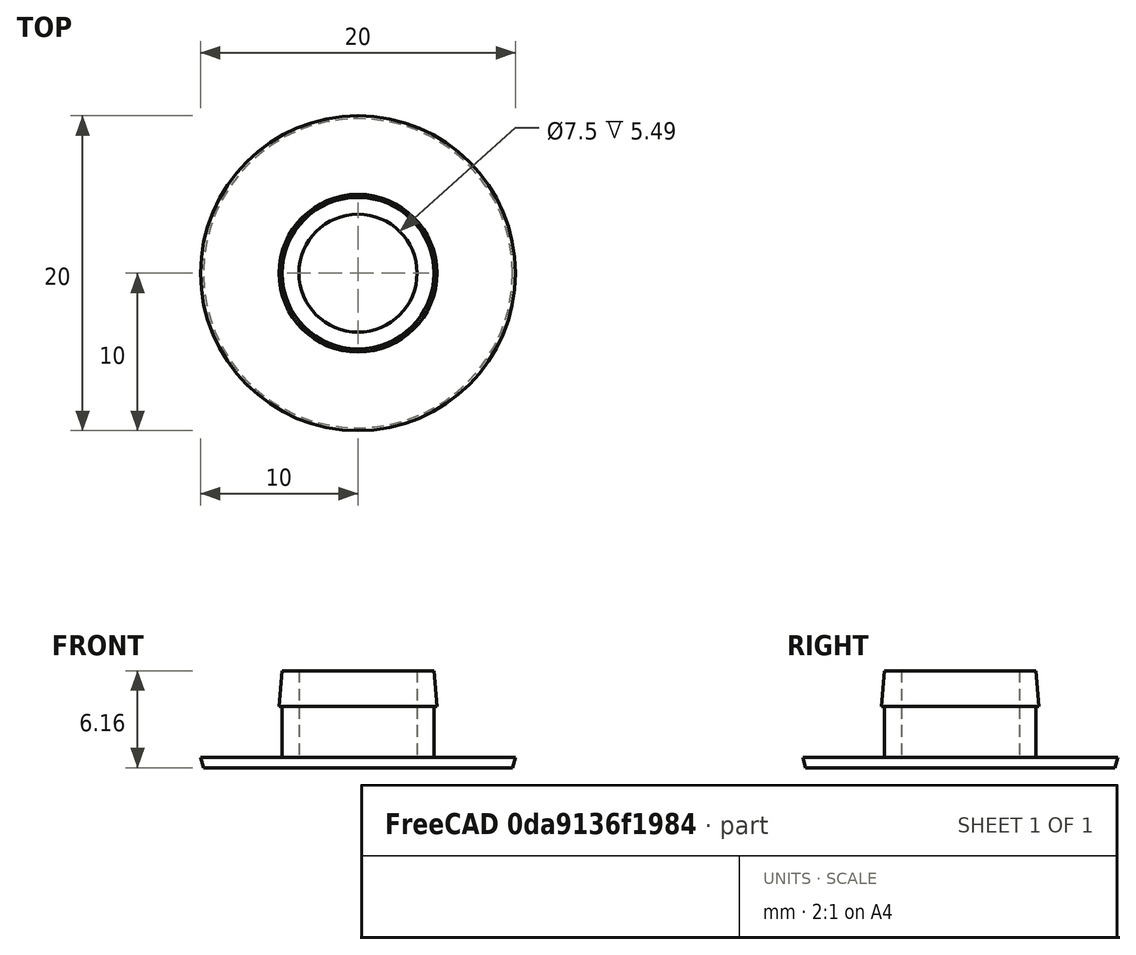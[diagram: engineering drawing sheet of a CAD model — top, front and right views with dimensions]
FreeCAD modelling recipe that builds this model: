
FCSTD DOCUMENT  (FreeCAD 0.21R33771 (Git))
Label: door_threshold_screw_cover_r1_9_3mm
License: Creative Commons Attribution
LicenseURL: http://creativecommons.org/licenses/by/3.0/
objects: Sketcher::SketchObject×1, PartDesign::Revolution×1, PartDesign::Body×1, Mesh::Feature×1
note: 4 computed .brp shape members not serialized (recipe doc carries the construction recipe); baked Part::Feature solids carry a one-line shape summary decoded from their .brp

FEATURE [Sketcher::SketchObject] Sketch
  FullyConstrained = false
  MapMode = 5
  Placement = pos=(0,0,0) rot=(1,0,0;1.5708rad)
  Support = -> [XZ_Plane]
  expr: .Constraints.hole_radius = 9.64 / 2
  expr: .Constraints.hole_radius_copy1 = .Constraints.hole_radius
  expr: .Constraints.hole_radius_copy2 = .Constraints.hole_radius
  expr: .Constraints.inner_hole_radius = 7.5 / 2
  expr: .Constraints.lid_thickness2 = .Constraints.lid_thickness1
  expr: .Constraints.max_outer_radius = 20 / 2
  sketch-geometry (11):
    g0: LineSegment StartX=0 StartY=0 StartZ=0 EndX=-4.82 EndY=0 EndZ=0
    g1: LineSegment StartX=-10 StartY=0.67 StartZ=0 EndX=-4.82 EndY=0.67 EndZ=0
    g2: LineSegment StartX=-4.82 StartY=0.67 StartZ=0 EndX=-4.82 EndY=3.91 EndZ=0
    g3: LineSegment StartX=-4.82 StartY=3.91 StartZ=0 EndX=-5.01 EndY=3.91 EndZ=0
    g4: LineSegment StartX=-5.01 StartY=3.91 StartZ=0 EndX=-4.82 EndY=6.16 EndZ=0
    g5: LineSegment StartX=-4.82 StartY=6.16 StartZ=0 EndX=-3.75 EndY=6.16 EndZ=0
    g6: LineSegment StartX=-3.75 StartY=6.16 StartZ=0 EndX=-3.75 EndY=2.26679 EndZ=0
    g7: LineSegment StartX=-3.75 StartY=2.26679 StartZ=0 EndX=0 EndY=2.26679 EndZ=0
    g8: LineSegment StartX=0 StartY=2.26679 StartZ=0 EndX=0 EndY=0 EndZ=0
    g9: LineSegment StartX=-4.82 StartY=0 StartZ=0 EndX=-9.82 EndY=0 EndZ=0
    g10: LineSegment StartX=-9.82 StartY=0 StartZ=0 EndX=-10 EndY=0.67 EndZ=0
  constraints (32):
    c: Coincident(g-1,g0)
    c: PointOnObject(g0,g-1)
    c: Horizontal(g1)
    c: Coincident(g1,g2)
    c: Vertical(g2)
    c: Coincident(g2,g3)
    c: Horizontal(g3)
    c: Coincident(g3,g4)
    c: DistanceX(g1,g0) = 10  'max_outer_radius'
    c: DistanceX(g0,g0) = 4.82  'hole_radius'
    c: DistanceX(g1,g0) = 4.82  'hole_radius_copy1'
    c: DistanceY(g0,g1) = 0.67  'lid_thickness1'
    c: Coincident(g4,g5)
    c: Horizontal(g5)
    c: Coincident(g5,g6)
    c: Vertical(g6)
    c: Coincident(g6,g7)
    c: Horizontal(g7)
    c: Coincident(g7,g8)
    c: DistanceY(g0,g7) = 0.67  'lid_thickness2'
    c: DistanceX(g6,g7) = 3.75  'inner_hole_radius'
    c: DistanceX(g3,g5) = 1.26  'shaft_thickness'
    c: Vertical(g8)
    c: Coincident(g8,g0)
    c: DistanceY(g0,g5) = 6.16  'depth2'
    c: DistanceY(g0,g2) = 3.91  'outer_lib_depth'
    c: DistanceX(g4,g7) = 4.82  'hole_radius_copy2'
    c: Horizontal(g9)
    c: Coincident(g9,g10)
    c: Coincident(g1,g10)
    c: Coincident(g9,g0)
    c: DistanceX(g9,g9) = 5  'top_cap_extension'
FEATURE [PartDesign::Revolution] Revolution
  Angle = 360
  Axis = (0,-2e-16,1)
  Base = (0,0,0)
  Placement = pos=(0,0,0) rot=(1,0,0;1.5708rad)
  Profile = -> Sketch
  ReferenceAxis = -> Sketch [V_Axis]
FEATURE [PartDesign::Body] Body
  Group = -> [Sketch,Revolution]
  Origin = -> Origin
  Tip = -> Revolution
FEATURE [Mesh::Feature] Mesh  label="Revolution (Meshed)"
